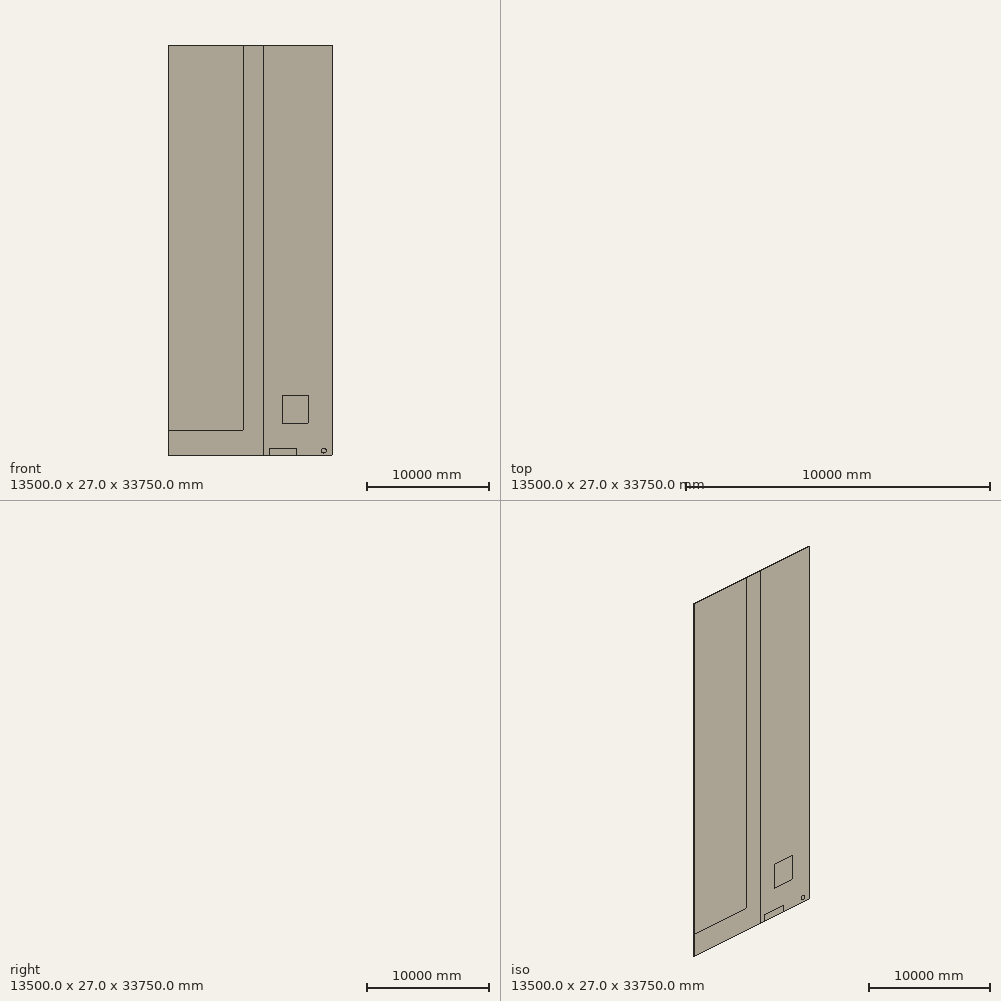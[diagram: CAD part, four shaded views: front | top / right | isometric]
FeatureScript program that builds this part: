
annotation { "Feature Type Name" : "Feature", "Feature Type Description" : "" }
export const myFeature = defineFeature(function(context is Context, id is Id, definition is map)
    precondition{}
    {
        {
            var Q0;
            Q0=qCreatedBy(makeId("Front.planeOp"),FACE);
            var sketch = newSketch(context, id + "F0", { "sketchPlane" : qUnion([Q0])});
            skLineSegment(sketch, "E0.0.1.0", {"start": v(6750, 3750) * mm, "end": v(-6750, 3750) * mm, "construction": true});
            skLineSegment(sketch, "E0.0.2.0", {"start": v(6750, 7500) * mm, "end": v(-6750, 7500) * mm, "construction": true});
            skLineSegment(sketch, "E0.0.3.0", {"start": v(6750, 11250) * mm, "end": v(-6750, 11250) * mm, "construction": true});
            skLineSegment(sketch, "E0.0.4.0", {"start": v(6750, 15000) * mm, "end": v(-6750, 15000) * mm, "construction": true});
            skLineSegment(sketch, "E0.0.5.0", {"start": v(6750, 18750) * mm, "end": v(-6750, 18750) * mm, "construction": true});
            skLineSegment(sketch, "E0.0.6.0", {"start": v(6750, 22500) * mm, "end": v(-6750, 22500) * mm, "construction": true});
            skLineSegment(sketch, "E0.0.7.0", {"start": v(6750, 26250) * mm, "end": v(-6750, 26250) * mm, "construction": true});
            skLineSegment(sketch, "E0.0.8.0", {"start": v(6750, 30000) * mm, "end": v(-6750, 30000) * mm, "construction": true});
            skLineSegment(sketch, "E0.0.9.0", {"start": v(6750, 33750) * mm, "end": v(-6750, 33750) * mm, "construction": true});
            skLineSegment(sketch, "E1.bottom", {"start": v(-6750, 33750) * mm, "end": v(-150, 33750) * mm});
            skLineSegment(sketch, "E2.top", {"start": v(6750, 33750) * mm, "end": v(1050, 33750) * mm});
            skLineSegment(sketch, "E3.0.1.0", {"start": v(6750, 0) * mm, "end": v(-6750, 0) * mm, "construction": true});
            skLineSegment(sketch, "E3.direction1", {"start": v(-6750, 3750) * mm, "end": v(-6725, 3750) * mm, "construction": true});
            skLineSegment(sketch, "E4", {"start": v(-6750, 33750) * mm, "end": v(-6750, 0) * mm});
            skLineSegment(sketch, "E5", {"start": v(6750, 33750) * mm, "end": v(6750, 0) * mm});
            skLineSegment(sketch, "E6", {"start": v(-6750, 0) * mm, "end": v(6750, 0) * mm});
            skLineSegment(sketch, "E7", {"start": v(-6750, 33750) * mm, "end": v(6750, 33750) * mm});
            skSolve(sketch);
        }
        {
            var Q0;
            Q0=qSketchRegion(id+"F0",true);
            extrude(context, id + "F1", {"entities" : qUnion([Q0]), "depth" : 25 * mm});
        }
        {
            var Q0;
            Q0=makeQuery(id+"F1.opExtrude","CAP_FACE",FACE,{"disambiguationData":[OSD([sQuery(id+"F0.wireOp",EDGE,"E4"),sQuery(id+"F0.wireOp",EDGE,"E5"),sQuery(id+"F0.wireOp",EDGE,"E6"),sQuery(id+"F0.wireOp",EDGE,"E7")])],"isStart":false});
            var sketch = newSketch(context, id + "F2", { "sketchPlane" : qUnion([Q0])});
            skLineSegment(sketch, "E8", {"start": v(-6750, 0) * mm, "end": v(6750, 0) * mm, "construction": true});
            skLineSegment(sketch, "E9.0.1.0", {"start": v(-6750, 3750) * mm, "end": v(6750, 3750) * mm, "construction": true});
            skLineSegment(sketch, "E9.0.2.0", {"start": v(-6750, 7500) * mm, "end": v(6750, 7500) * mm, "construction": true});
            skLineSegment(sketch, "E9.0.3.0", {"start": v(-6750, 11250) * mm, "end": v(6750, 11250) * mm, "construction": true});
            skLineSegment(sketch, "E9.0.4.0", {"start": v(-6750, 15000) * mm, "end": v(6750, 15000) * mm, "construction": true});
            skLineSegment(sketch, "E9.0.5.0", {"start": v(-6750, 18750) * mm, "end": v(6750, 18750) * mm, "construction": true});
            skLineSegment(sketch, "E9.0.6.0", {"start": v(-6750, 22500) * mm, "end": v(6750, 22500) * mm, "construction": true});
            skLineSegment(sketch, "E9.0.7.0", {"start": v(-6750, 26250) * mm, "end": v(6750, 26250) * mm, "construction": true});
            skLineSegment(sketch, "E9.direction1", {"start": v(-6750, 0) * mm, "end": v(-6725, 0) * mm, "construction": true});
            skLineSegment(sketch, "E9.direction2", {"start": v(-6750, 0) * mm, "end": v(-6750, 3750) * mm, "construction": true});
            skLineSegment(sketch, "E10.0.0.8", {"start": v(-6750, 30000) * mm, "end": v(6750, 30000) * mm, "construction": true});
            skLineSegment(sketch, "E10.0.0.9", {"start": v(-6750, 33750) * mm, "end": v(6750, 33750) * mm, "construction": true});
            skLineSegment(sketch, "E11.bottom", {"start": v(-6750, 33750) * mm, "end": v(-550, 33750) * mm});
            skLineSegment(sketch, "E11.top", {"start": v(-6750, 2100) * mm, "end": v(-550, 2100) * mm});
            skLineSegment(sketch, "E11.left", {"start": v(-6750, 33750) * mm, "end": v(-6750, 2100) * mm});
            skLineSegment(sketch, "E11.right", {"start": v(-550, 33750) * mm, "end": v(-550, 2100) * mm});
            skLineSegment(sketch, "E12.bottom", {"start": v(6750, 0) * mm, "end": v(1050, 0) * mm});
            skLineSegment(sketch, "E12.top", {"start": v(6750, 33750) * mm, "end": v(1050, 33750) * mm});
            skLineSegment(sketch, "E12.left", {"start": v(6750, 0) * mm, "end": v(6750, 33750) * mm});
            skLineSegment(sketch, "E12.right", {"start": v(1050, 0) * mm, "end": v(1050, 33750) * mm});
            skSolve(sketch);
        }
        {
            var Q0;
            Q0=qSketchRegion(id+"F2",true);
            extrude(context, id + "F3", {"entities" : qUnion([Q0]), "operationType" : NewBodyOperationType.ADD, "depth" : 1 * mm});
        }
        {
            var Q0;
            Q0=makeQuery(id+"F3.opExtrude","CAP_FACE",FACE,{"disambiguationData":[OSD([sQuery(id+"F2.wireOp",EDGE,"E12.bottom"),sQuery(id+"F2.wireOp",EDGE,"E12.top"),sQuery(id+"F2.wireOp",EDGE,"E12.left"),sQuery(id+"F2.wireOp",EDGE,"E12.right")])],"isStart":false});
            var sketch = newSketch(context, id + "F4", { "sketchPlane" : qUnion([Q0])});
            skLineSegment(sketch, "E13", {"start": v(6750, 0) * mm, "end": v(-6750, 0) * mm, "construction": true});
            skLineSegment(sketch, "E14.0.1.0", {"start": v(6750, 3750) * mm, "end": v(-6750, 3750) * mm, "construction": true});
            skLineSegment(sketch, "E14.0.2.0", {"start": v(6750, 7500) * mm, "end": v(-6750, 7500) * mm, "construction": true});
            skLineSegment(sketch, "E14.0.3.0", {"start": v(6750, 11250) * mm, "end": v(-6750, 11250) * mm, "construction": true});
            skLineSegment(sketch, "E14.0.4.0", {"start": v(6750, 15000) * mm, "end": v(-6750, 15000) * mm, "construction": true});
            skLineSegment(sketch, "E14.0.5.0", {"start": v(6750, 18750) * mm, "end": v(-6750, 18750) * mm, "construction": true});
            skLineSegment(sketch, "E14.0.6.0", {"start": v(6750, 22500) * mm, "end": v(-6750, 22500) * mm, "construction": true});
            skLineSegment(sketch, "E14.0.7.0", {"start": v(6750, 26250) * mm, "end": v(-6750, 26250) * mm, "construction": true});
            skLineSegment(sketch, "E14.0.8.0", {"start": v(6750, 30000) * mm, "end": v(-6750, 30000) * mm, "construction": true});
            skLineSegment(sketch, "E14.0.9.0", {"start": v(6750, 33750) * mm, "end": v(-6750, 33750) * mm, "construction": true});
            skLineSegment(sketch, "E14.direction1", {"start": v(-6750, 0) * mm, "end": v(-6725, 0) * mm, "construction": true});
            skLineSegment(sketch, "E14.direction2", {"start": v(-6750, 0) * mm, "end": v(-6750, 3750) * mm, "construction": true});
            skLineSegment(sketch, "E15.bottom", {"start": v(1550, 0) * mm, "end": v(3750, 0) * mm});
            skLineSegment(sketch, "E15.top", {"start": v(1550, 600) * mm, "end": v(3750, 600) * mm});
            skLineSegment(sketch, "E15.left", {"start": v(1550, 0) * mm, "end": v(1550, 600) * mm});
            skLineSegment(sketch, "E15.right", {"start": v(3750, 0) * mm, "end": v(3750, 600) * mm});
            skCircle(sketch, "E16", {"center": v(6050, 400) * mm, "radius": 200 * mm});
            skLineSegment(sketch, "E17.bottom", {"start": v(2650, 4950) * mm, "end": v(4750, 4950) * mm});
            skLineSegment(sketch, "E17.top", {"start": v(2650, 2650) * mm, "end": v(4750, 2650) * mm});
            skLineSegment(sketch, "E17.left", {"start": v(2650, 4950) * mm, "end": v(2650, 2650) * mm});
            skLineSegment(sketch, "E17.right", {"start": v(4750, 4950) * mm, "end": v(4750, 2650) * mm});
            skLineSegment(sketch, "E18", {"start": v(-6750, 33750) * mm, "end": v(-6725, 0) * mm, "construction": true});
            skLineSegment(sketch, "E19", {"start": v(6750, 33750) * mm, "end": v(6750, 0) * mm, "construction": true});
            skSolve(sketch);
        }
        {
            var Q0;
            Q0 = qSketchRegion(id + "F4", true);
            extrude(context, id + "F5", {"entities" : qUnion([Q0]), "operationType" : NewBodyOperationType.ADD, "depth" : 1 * mm});
        }
    });
